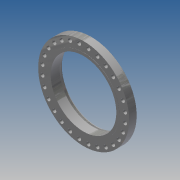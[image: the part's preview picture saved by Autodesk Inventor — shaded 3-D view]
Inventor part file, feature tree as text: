
AUTODESK INVENTOR PART (.ipt)
format: ipt  version: 2017.3 (Build 213257000, 257)  size: 339,968 bytes
history: native  units: in
note: dims shown in document units (in); Inventor stores cm internally (conversion verified against a paired STEP export)
features: sketch x6, extrude x4, chamfer x4, fillet x2, hole x1, pattern_circular x1, revolve x1, projected_geometry x1
ambient origin geometry x8: Origin, YZ Plane, XZ Plane, XY Plane, X Axis, Y Axis, Z Axis, Center Point
bodies: Solid1 (feature_tree)
feature tree (20):
  extrude  "Extrusion1"  Depth=31.0in
  extrude  "Extrusion2"  Depth=3.625in
  extrude  "Extrusion3"  Depth=0.0625in
  extrude  "Extrusion9"  Depth=19.625in
  hole  "Hole1"  [1 undecoded]
  chamfer  "Chamfer3"  Distance=0.0625in
  pattern_circular  "Circular Pattern1"  [2 undecoded]
  chamfer  "Chamfer2"  Distance=0.0312in Angle=45.0deg
  fillet  "Fillet2"  Radius=0.0625in
  chamfer  "Chamfer4"  Distance=34.0in
  revolve  "Revolution3"  [1 undecoded]
  fillet  "Fillet7"  Radius=0.125in
  chamfer  "Chamfer8"  Distance=0.25in
  sketch  "Sketch1"  dims[d0=43.0in d1=31.0in]
  sketch  "Sketch2"  dims[d2=3.625in d3=0.0in d4=33.75in]
  sketch  "Sketch3"  dims[d5=0.0625in d6=0.0in d7=34.75in]
  sketch  "Sketch4"  dims[d8=2.4375in d9=0.0in d13=19.625in]
  sketch  "Sketch12"  dims[d14=0.0442in]
  sketch  "Sketch15"  dims[d15=1.875in d16=0.75in d17=0.375in d18=0.25in d19=0.5635in d20=1.0in d21=0.8108in d22=11.0236in d23=360.0deg d25=0.0625in d26=0.125in d27=0.0687in d29=0.4375in d30=0.0312in d31=0.125in d32=45.0deg d33=0.0625in d34=0.125in d35=45.0deg d98=34.0in d99=0.4375in d100=0.125in d101=0.25in d102=0.2577in d103=0.5in d104=0.875in d105=0.2893in d106=31.375in d108=90.0deg d109=0.0312in d110=0.0312in d111=0.125in d112=45.0deg d120=1.0in d129=1.0in d130=0.0in d134=0.0625in d135=0.1718in]
  projected_geometry  "Projected Loop1"
note: 4 required parameter values undecoded (feature->parameter linkage not recoverable at this tier; creation-order binding heuristic only, values carry confidence <= 0.55)